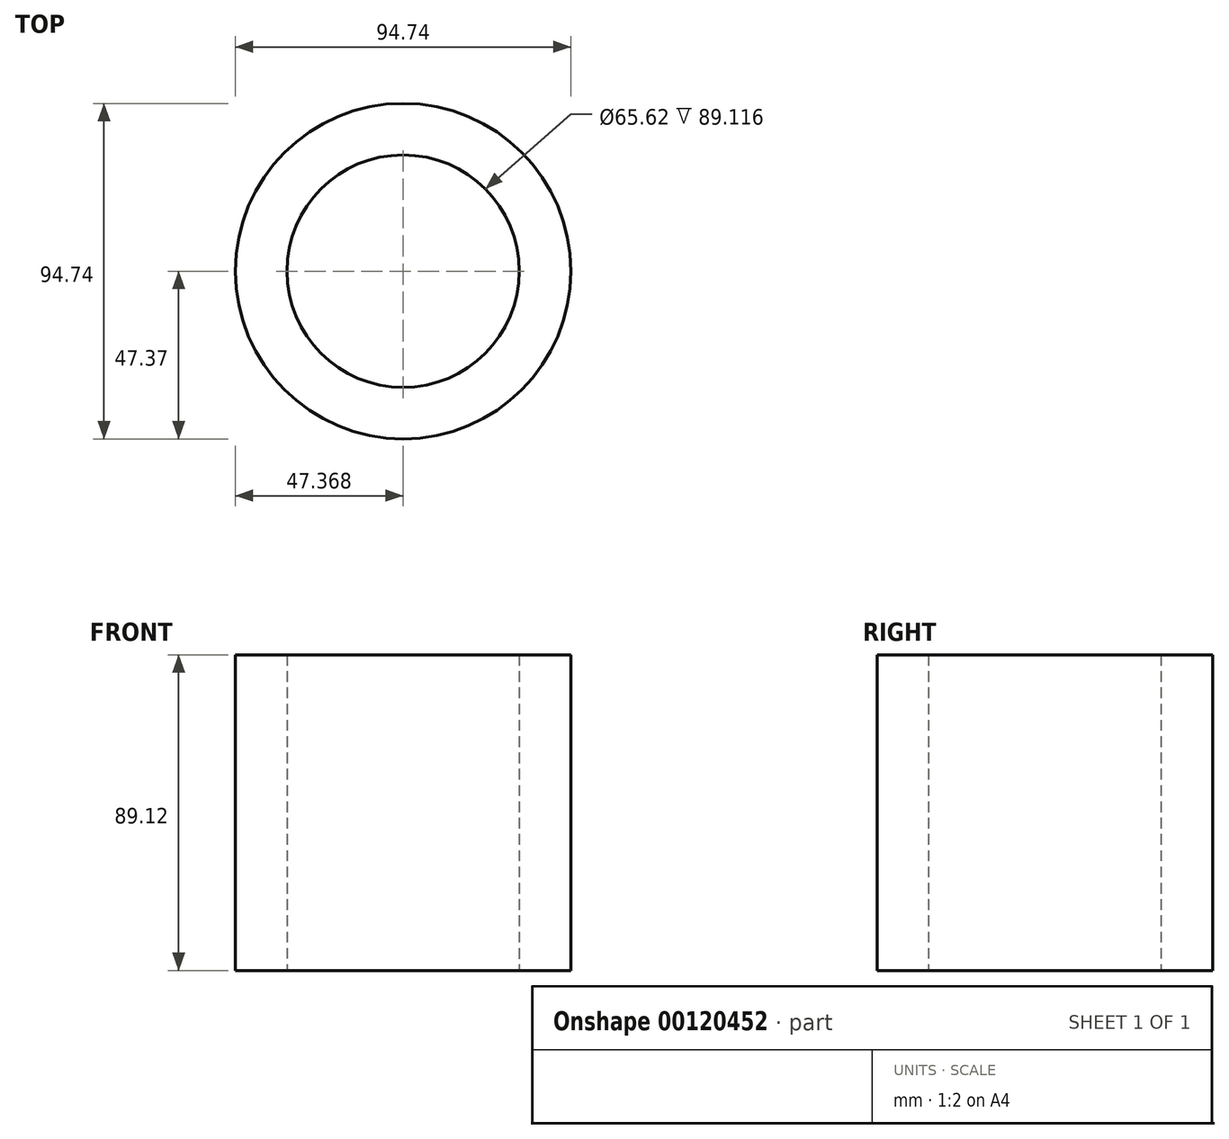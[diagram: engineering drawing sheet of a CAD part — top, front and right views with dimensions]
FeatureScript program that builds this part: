
annotation { "Feature Type Name" : "Feature", "Feature Type Description" : "" }
export const myFeature = defineFeature(function(context is Context, id is Id, definition is map)
    precondition{}
    {
        {
            var Q0;
            Q0=qCreatedBy(makeId("Top.planeOp"),FACE);
            var sketch = newSketch(context, id + "F0", { "sketchPlane" : qUnion([Q0])});
            skCircle(sketch, "E0", {"center": v(-12.48, 0) * mm, "radius": 47.37 * mm});
            skCircle(sketch, "E1", {"center": v(-12.48, 0) * mm, "radius": 32.81 * mm});
            skSolve(sketch);
        }
        {
            var Q0;
            Q0=makeQuery(id+"F0.imprint","IMPRINT",FACE,{"disambiguationData":[TD([[makeQuery(id+"F0.imprint","IMPRINT",EDGE,{"derivedFrom":sQuery(id+"F0.wireOp",EDGE,"E0")}),1.0]])]});
            extrude(context, id + "F1", {"entities" : qUnion([Q0]), "depth" : 89.12 * mm});
        }
    });
